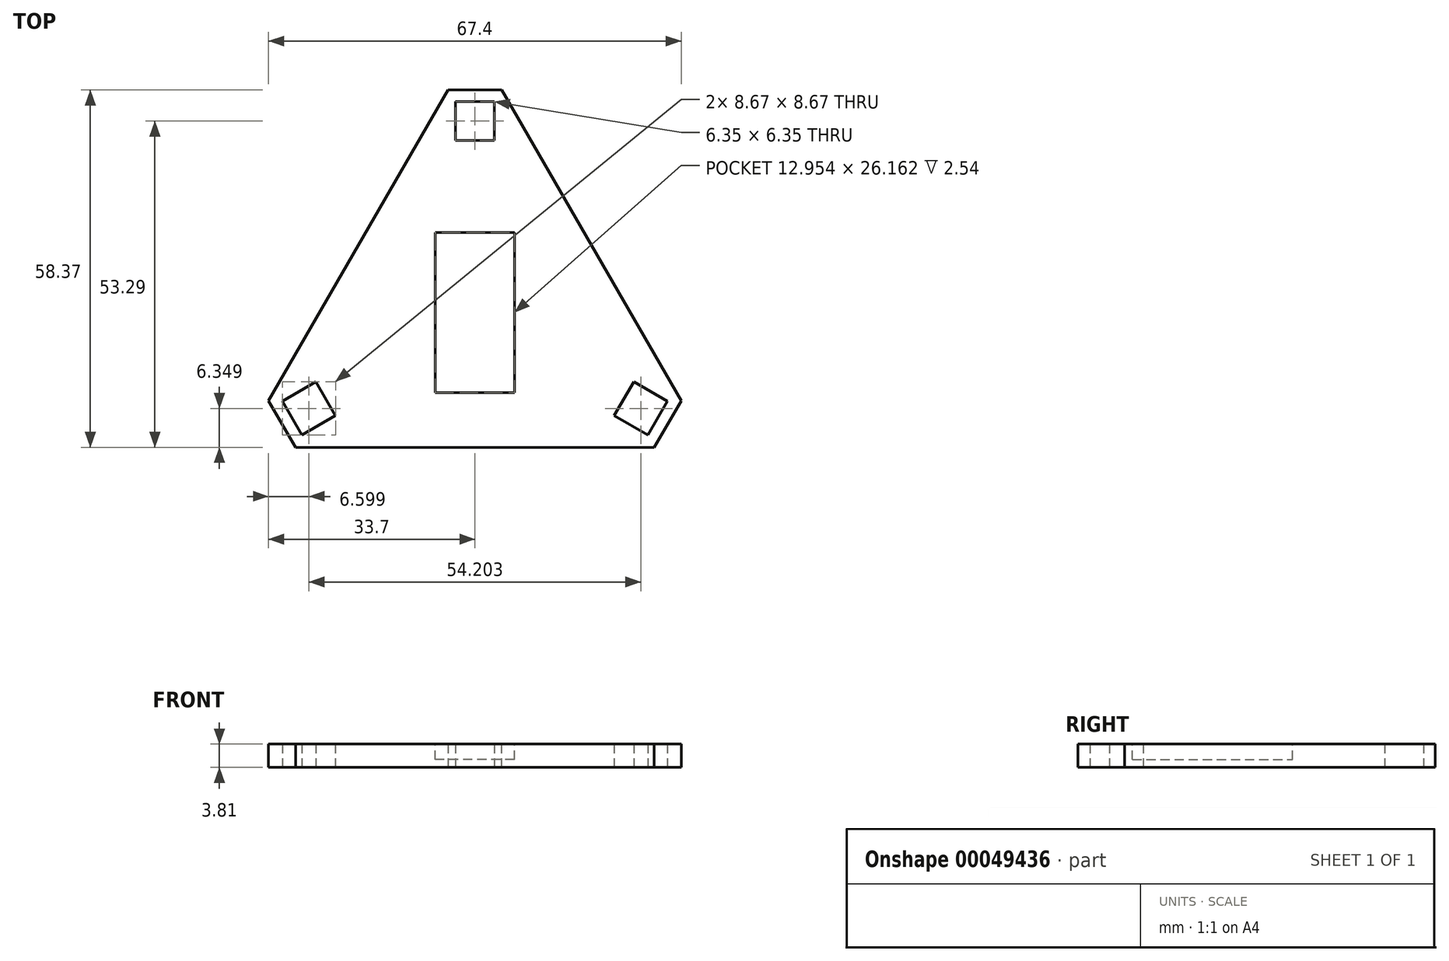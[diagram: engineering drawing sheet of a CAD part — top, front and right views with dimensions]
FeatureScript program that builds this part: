
annotation { "Feature Type Name" : "Feature", "Feature Type Description" : "" }
export const myFeature = defineFeature(function(context is Context, id is Id, definition is map)
    precondition{}
    {
        {
            var Q0;
            Q0=qCreatedBy(makeId("Top.planeOp"),FACE);
            var sketch = newSketch(context, id + "F0", { "sketchPlane" : qUnion([Q0])});
            skLineSegment(sketch, "E0", {"start": v(0, 0) * mm, "end": v(38.1, -66) * mm});
            skLineSegment(sketch, "E1", {"start": v(38.1, -66) * mm, "end": v(-38.1, -66) * mm});
            skLineSegment(sketch, "E2", {"start": v(-38.1, -66) * mm, "end": v(0, 0) * mm});
            skLineSegment(sketch, "E3", {"start": v(0, 0) * mm, "end": v(0, -66) * mm, "construction": true});
            skSolve(sketch);
        }
        {
            var Q0;
            Q0=makeQuery(id+"F0.imprint","IMPRINT",FACE,{"disambiguationData":[TD([[makeQuery(id+"F0.imprint","IMPRINT",EDGE,{"derivedFrom":sQuery(id+"F0.wireOp",EDGE,"E0")}),-1.0]])]});
            extrude(context, id + "F1", {"entities" : qUnion([Q0]), "depth" : 3.8 * mm});
        }
        {
            var Q0;
            Q0=makeQuery(id+"F1.opExtrude","CAP_FACE",FACE,{"disambiguationData":[OSD([sQuery(id+"F0.wireOp",EDGE,"E0"),sQuery(id+"F0.wireOp",EDGE,"E1"),sQuery(id+"F0.wireOp",EDGE,"E2")])],"isStart":false});
            var sketch = newSketch(context, id + "F2", { "sketchPlane" : qUnion([Q0])});
            skLineSegment(sketch, "E4", {"start": v(0, -44) * mm, "end": v(0, -66) * mm, "construction": true});
            skLineSegment(sketch, "E5.rect.bottom", {"start": v(6.48, -57.08) * mm, "end": v(-6.48, -57.08) * mm});
            skLineSegment(sketch, "E5.rect.top", {"start": v(6.48, -30.91) * mm, "end": v(-6.48, -30.91) * mm});
            skLineSegment(sketch, "E5.rect.left", {"start": v(6.48, -57.08) * mm, "end": v(6.48, -30.91) * mm});
            skLineSegment(sketch, "E5.rect.right", {"start": v(-6.48, -57.08) * mm, "end": v(-6.48, -30.91) * mm});
            skPoint(sketch, "E5.rect.middle", {"position": v(0, -44) * mm});
            skLineSegment(sketch, "E6", {"start": v(38.1, -66) * mm, "end": v(0, -44) * mm, "construction": true});
            skLineSegment(sketch, "E7", {"start": v(0, -44) * mm, "end": v(19.05, -33) * mm, "construction": true});
            skPoint(sketch, "E8.orphan", {"position": v(-19.05, -33) * mm});
            skPoint(sketch, "E9.orphan", {"position": v(0, 0) * mm});
            skSolve(sketch);
        }
        {
            var Q0;
            Q0=qSketchRegion(id+"F2",true);
            extrude(context, id + "F3", {"entities" : qUnion([Q0]), "operationType" : NewBodyOperationType.REMOVE, "oppositeDirection" : true, "depth" : 2.54 * mm});
        }
        {
            var Q0;
            Q0=qCreatedBy(makeId("Top.planeOp"),FACE);
            var sketch = newSketch(context, id + "F4", { "sketchPlane" : qUnion([Q0])});
            skLineSegment(sketch, "E10", {"start": v(0, 0) * mm, "end": v(0, -12.7) * mm, "construction": true});
            skLineSegment(sketch, "E11.1.0", {"start": v(-38.1, -66) * mm, "end": v(-27.1, -59.64) * mm, "construction": true});
            skLineSegment(sketch, "E11.2.0", {"start": v(38.1, -66) * mm, "end": v(27.1, -59.64) * mm, "construction": true});
            skPoint(sketch, "E11.center", {"position": v(0, -44) * mm});
            skLineSegment(sketch, "E12.rect.bottom", {"start": v(3.18, -15.88) * mm, "end": v(-3.18, -15.88) * mm});
            skLineSegment(sketch, "E12.rect.top", {"start": v(3.18, -9.53) * mm, "end": v(-3.17, -9.53) * mm});
            skLineSegment(sketch, "E12.rect.left", {"start": v(3.18, -15.88) * mm, "end": v(3.18, -9.53) * mm});
            skLineSegment(sketch, "E12.rect.right", {"start": v(-3.18, -15.88) * mm, "end": v(-3.17, -9.53) * mm});
            skPoint(sketch, "E12.rect.middle", {"position": v(0, -12.7) * mm});
            skLineSegment(sketch, "E13.1.0", {"start": v(-31.44, -58.48) * mm, "end": v(-28.26, -63.98) * mm});
            skLineSegment(sketch, "E13.1.1", {"start": v(-25.94, -55.3) * mm, "end": v(-31.44, -58.48) * mm});
            skLineSegment(sketch, "E13.1.2", {"start": v(-25.94, -55.3) * mm, "end": v(-22.76, -60.8) * mm});
            skLineSegment(sketch, "E13.1.3", {"start": v(-22.76, -60.8) * mm, "end": v(-28.26, -63.98) * mm});
            skLineSegment(sketch, "E13.2.0", {"start": v(28.26, -63.98) * mm, "end": v(31.44, -58.48) * mm});
            skLineSegment(sketch, "E13.2.1", {"start": v(22.76, -60.8) * mm, "end": v(28.26, -63.98) * mm});
            skLineSegment(sketch, "E13.2.2", {"start": v(22.76, -60.8) * mm, "end": v(25.94, -55.3) * mm});
            skLineSegment(sketch, "E13.2.3", {"start": v(25.94, -55.3) * mm, "end": v(31.44, -58.48) * mm});
            skSolve(sketch);
        }
        {
            var Q0;
            Q0=qSketchRegion(id+"F4",true);
            extrude(context, id + "F5", {"entities" : qUnion([Q0]), "operationType" : NewBodyOperationType.REMOVE, "depth" : 3.8 * mm});
        }
        {
            var Q0;
            Q0=makeQuery(id+"F1.opExtrude","SWEPT_EDGE",EDGE,{"disambiguationData":[OSD([sQuery(id+"F0.wireOp",EDGE,"E1"),sQuery(id+"F0.wireOp",EDGE,"E2")])]});
            var Q1;
            Q1=makeQuery(id+"F1.opExtrude","SWEPT_EDGE",EDGE,{"disambiguationData":[OSD([sQuery(id+"F0.wireOp",EDGE,"E0"),sQuery(id+"F0.wireOp",EDGE,"E2")])]});
            var Q2;
            Q2=makeQuery(id+"F1.opExtrude","SWEPT_EDGE",EDGE,{"disambiguationData":[OSD([sQuery(id+"F0.wireOp",EDGE,"E0"),sQuery(id+"F0.wireOp",EDGE,"E1")])]});
            chamfer(context, id + "F6", {"entities" : qUnion([Q0, Q1, Q2]), "width" : 5.08 * mm, "tangentPropagation" : true});
        }
    });
